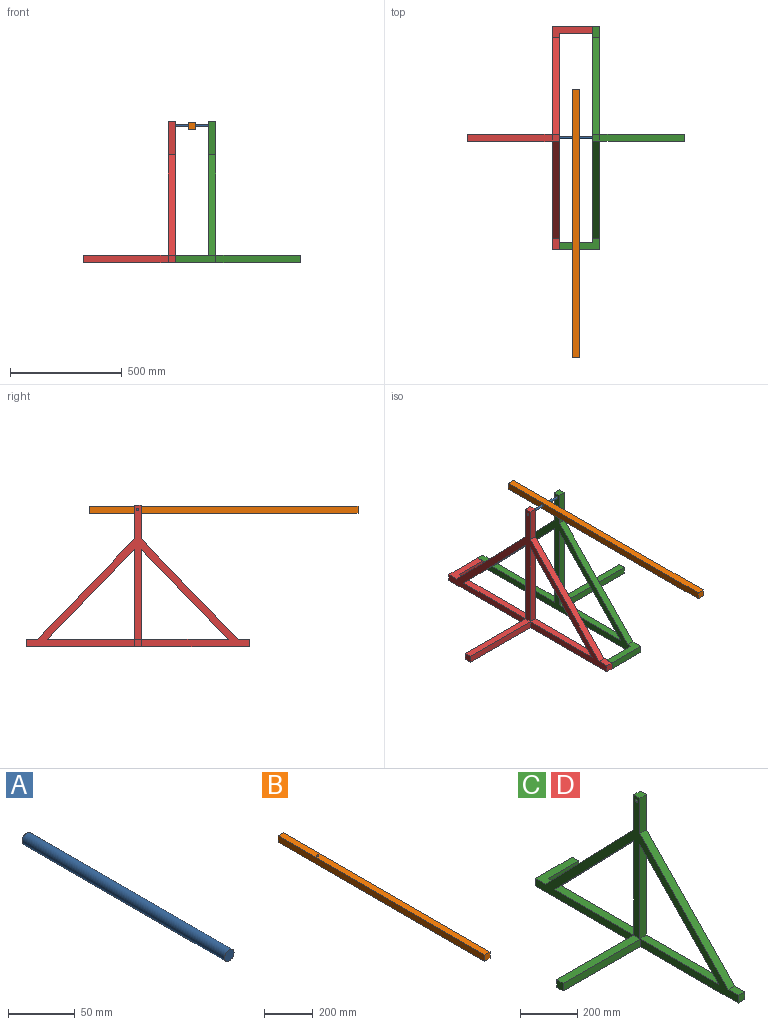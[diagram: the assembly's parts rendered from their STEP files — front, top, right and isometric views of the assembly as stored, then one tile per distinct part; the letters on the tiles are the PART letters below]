
ASSEMBLY  parts=4 mates=3
PART A: 3 faces, bbox 10x214x10 mm
  f0: cylinder r=5mm len=214mm, axis (0,1,0), area 6723mm2, adj f1,f2
  f1: plane 10x10mm, normal (0,-1,0), area 78.5mm2, adj f0
  f2: plane 10x10mm, normal (0,1,0), area 78.5mm2, adj f0
PART B: 7 faces, bbox 32x1200x32 mm
  f0: plane 1200x32mm, normal (0,0,1), area 38321.5mm2, adj f1,f3,f4,f5,f6
  f1: plane 1200x32mm, normal (-1,0,0), area 38400mm2, adj f0,f2,f4,f5
  f2: plane 1200x32mm, normal (0,0,-1), area 38321.5mm2, adj f1,f3,f4,f5,f6
  f3: plane 1200x32mm, normal (1,0,0), area 38400mm2, adj f0,f2,f4,f5
  f4: plane 32x32mm, normal (0,-1,0), area 1024mm2, adj f0,f1,f2,f3
  f5: plane 32x32mm, normal (0,1,0), area 1024mm2, adj f0,f1,f2,f3
  f6: cylinder r=5mm len=32mm, axis (0,0,1), area 1005.3mm2, adj f0,f2
PART C: 24 faces, bbox 562x1000x632 mm
  f0: plane 390.38x32mm, normal (0,0,1), area 12492.3mm2, adj f5,f7,f11,f17
  f1: plane 150x32mm, normal (0,1,0), area 4800mm2, adj f5,f7,f13,f16
  f2: plane 50x32mm, normal (0,0,1), area 1600mm2, adj f5,f7,f9,f14
  f3: plane 150x32mm, normal (0,-1,0), area 4800mm2, adj f5,f7,f13,f14
  f4: plane 182x50mm, normal (0,0,1), area 6400mm2, adj f5,f7,f10,f16,f18,f19
  f5: plane 968x632mm, normal (1,0,0), area 87036.3mm2, adj f0,f1,f2,f3,f4,f6,f8,f9
  f6: plane 420.61x412mm, normal (0,0,1), area 24652.3mm2, adj f5,f7,f12,f15,f20,f21,f22
  f7: plane 1000x632mm, normal (-1,0,0), area 87036.3mm2, adj f0,f1,f2,f3,f4,f6,f8,f9
  f8: plane 1000x562mm, normal (0,0,-1), area 48960mm2, adj f5,f7,f9,f10,f18,f19,f20,f21
  f9: plane 32x32mm, normal (0,-1,0), area 1024mm2, adj f2,f5,f7,f8
  f10: plane 182x32mm, normal (0,1,0), area 5824mm2, adj f4,f7,f8,f19
  f11: plane 403.95x32mm, normal (0,1,0), area 12926.5mm2, adj f0,f5,f7,f17
  f12: plane 403.95x32mm, normal (0,-1,0), area 12926.5mm2, adj f5,f6,f7,f15
  f13: plane 32x30.23mm, normal (0,0,1), area 967.3mm2, adj f1,f3,f5,f7
  f14: plane 450x434.89mm, normal (0,-0.72,0.69), area 20025.6mm2, adj f2,f3,f5,f7
  f15: plane 403.95x390.38mm, normal (0,0.72,-0.69), area 17976.4mm2, adj f5,f6,f7,f12
  f16: plane 450x434.89mm, normal (0,0.72,0.69), area 20025.6mm2, adj f1,f4,f5,f7
  f17: plane 403.95x390.38mm, normal (0,-0.72,-0.69), area 17976.4mm2, adj f0,f5,f7,f11
  f18: plane 150x32mm, normal (0,-1,0), area 4800mm2, adj f4,f5,f8,f19
  f19: plane 32x32mm, normal (1,0,0), area 1024mm2, adj f4,f8,f10,f18
  f20: plane 380x32mm, normal (0,1,0), area 12160mm2, adj f6,f7,f8,f22
  f21: plane 380x32mm, normal (0,-1,0), area 12160mm2, adj f6,f7,f8,f22
  f22: plane 32x32mm, normal (-1,0,0), area 1024mm2, adj f6,f8,f20,f21
  f23: cylinder r=5mm len=32mm, axis (1,0,0), area 1005.3mm2, adj f5,f7
PART D: same geometry as C
PLACE A rot(axis=(-0.58,-0.58,-0.58),120deg) t=(114.87,-99.51,42.08)mm
PLACE B rot(axis=(0,-1,0),90deg) t=(212.34,293.83,-160.68)mm
PLACE C rot(axis=(0,0,-1),180deg) t=(98.87,79.06,-366.63)mm
PLACE D rot(axis=(0,0,1),0deg) t=(-83.13,79.06,-366.63)mm
MATE revolute A.f0 <-> B.f6  axis (1,0,0) through (7.87,79.06,230.45)mm
MATE revolute A.f0 <-> C.f23  axis (1,0,0) through (114.87,79.06,230.45)mm
MATE fastened D.f5 <-> C.f19  axis (-1,0,0) through (-67.13,-420.94,-350.63)mm
